# Revit family: 304_Frese Alpha HP DN15-50
name_source: partatom
category: Pipe Accessories
units: mm (PartAtom-declared; Revit-internal decimal feet)

## family parameters
Always vertical = Yes
Cut with Voids When Loaded = No
Part Type = Valve - Breaks Into
Round Connector Dimension = Use Diameter
Shared = No
Work Plane-Based = No

## types (7) — shared parameters
CAT0 = Yes
Description = Automatic balancing valve
L2D = 77 mm
L2D_Min = 3048 mm
Manufacturer = Frese A/S
QmdConnectorList = 301;D;302;D
URL = https://www.frese.eu
W2D = 15 mm  [stored 0.0492126 ft]
magiPartTypeId = 304
magiProductFamilyId = Frese Alpha HP DN15-50

## per-type parameters (varying)
| type | D | D2 | D32 | D4 | D42 | D5 | D6 | H1 | H2 | H2__ve | H3 | H4 | H5 | H6 | L1 | L1__ve | L2 | L3 | L4 | LL | S |
| Frese ALPHA DN15 HP | 15 mm | 29 mm  [stored 0.0951444 ft] | 11 mm | 17 mm | 6 mm  [stored 0.019685 ft] | 18 mm  [stored 0.0590551 ft] | 14 mm  [stored 0.0459318 ft] | 26 mm  [stored 0.0853018 ft] | 68 mm | -68 mm | 8 mm  [stored 0.0262467 ft] | 54 mm | 73 mm | 19 mm  [stored 0.062336 ft] | 19 mm  [stored 0.062336 ft] | -19 mm | 39 mm  [stored 0.127953 ft] | 0 mm  [stored 0 ft] | 29 mm  [stored 0.0951444 ft] | 39 mm  [stored 0.127953 ft] | 23 mm  [stored 0.0754593 ft] |
| Frese ALPHA DN20 HP | 20 mm | 39 mm  [stored 0.127953 ft] | 14 mm  [stored 0.0459318 ft] | 22 mm  [stored 0.0721785 ft] | 9 mm  [stored 0.0295276 ft] | 23 mm  [stored 0.0754593 ft] | 19 mm  [stored 0.062336 ft] | 32 mm  [stored 0.104987 ft] | 68 mm | -68 mm | 8 mm  [stored 0.0262467 ft] | 54 mm | 73 mm | 19 mm  [stored 0.062336 ft] | 19 mm  [stored 0.062336 ft] | -19 mm | 39 mm  [stored 0.127953 ft] | 4 mm  [stored 0.0131234 ft] | 29 mm  [stored 0.0951444 ft] | 39 mm  [stored 0.127953 ft] | 30 mm  [stored 0.0984252 ft] |
| Frese ALPHA DN25 HP | 25 mm | 39 mm  [stored 0.127953 ft] | 14 mm  [stored 0.0459318 ft] | 28 mm  [stored 0.0918635 ft] | 12 mm  [stored 0.0393701 ft] | 24 mm  [stored 0.0787402 ft] | 19 mm  [stored 0.062336 ft] | 35 mm | 68 mm | -68 mm | 8 mm  [stored 0.0262467 ft] | 54 mm | 73 mm | 19 mm  [stored 0.062336 ft] | 19 mm  [stored 0.062336 ft] | -19 mm | 39 mm  [stored 0.127953 ft] | 5 mm  [stored 0.0164042 ft] | 29 mm  [stored 0.0951444 ft] | 39 mm  [stored 0.127953 ft] | 38 mm  [stored 0.124672 ft] |
| Frese ALPHA DN25L HP | 25 mm | 39 mm  [stored 0.127953 ft] | 14 mm  [stored 0.0459318 ft] | 28 mm  [stored 0.0918635 ft] | 12 mm  [stored 0.0393701 ft] | 24 mm  [stored 0.0787402 ft] | 19 mm  [stored 0.062336 ft] | 40 mm  [stored 0.131234 ft] | 105 mm | -105 mm | 12 mm  [stored 0.0393701 ft] | 79 mm | 110 mm | 31 mm | 31 mm | -31 mm | 62 mm | 2 mm  [stored 0.00656168 ft] | 45 mm  [stored 0.147638 ft] | 62 mm | 38 mm  [stored 0.124672 ft] |
| Frese ALPHA DN32 HP | 32 mm | 48 mm  [stored 0.15748 ft] | 14 mm  [stored 0.0459318 ft] | 35 mm | 16 mm  [stored 0.0524934 ft] | 29 mm  [stored 0.0951444 ft] | 19 mm  [stored 0.062336 ft] | 46 mm | 105 mm | -105 mm | 12 mm  [stored 0.0393701 ft] | 79 mm | 110 mm | 31 mm | 31 mm | -31 mm | 62 mm | 1 mm  [stored 0.00328084 ft] | 45 mm  [stored 0.147638 ft] | 62 mm | 48 mm  [stored 0.15748 ft] |
| Frese ALPHA DN40 HP | 40 mm | 56 mm | 17 mm | 44 mm  [stored 0.144357 ft] | 20 mm  [stored 0.0656168 ft] | 34 mm  [stored 0.111549 ft] | 22 mm  [stored 0.0721785 ft] | 53 mm | 105 mm | -105 mm | 12 mm  [stored 0.0393701 ft] | 79 mm | 110 mm | 31 mm | 31 mm | -31 mm | 62 mm | 4 mm  [stored 0.0131234 ft] | 45 mm  [stored 0.147638 ft] | 62 mm | 56 mm |
| Frese ALPHA DN50 HP | 50 mm | 60 mm | 18 mm  [stored 0.0590551 ft] | 55 mm | 26 mm  [stored 0.0853018 ft] | 36 mm  [stored 0.11811 ft] | 24 mm  [stored 0.0787402 ft] | 60 mm | 105 mm | -105 mm | 12 mm  [stored 0.0393701 ft] | 79 mm | 110 mm | 31 mm | 31 mm | -31 mm | 62 mm | 6 mm  [stored 0.019685 ft] | 45 mm  [stored 0.147638 ft] | 62 mm | 60 mm |

note: column(s) folded — value = type name in every type: MC Product Code, magiProductId

note: [stored X ft] marks values corroborated as IEEE doubles in the binary element streams (Revit-internal decimal feet)

## geometry (parser evidence)
native form markers: Sweep x1
no freeform markers — native parametric forms only
